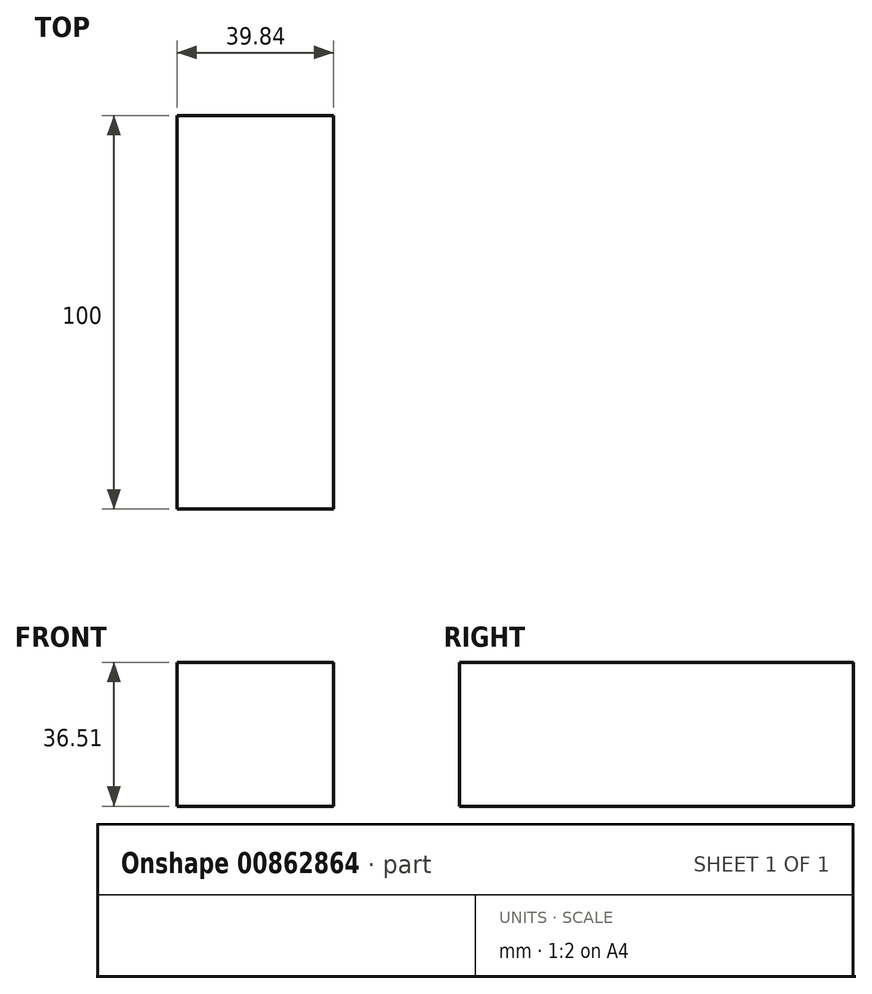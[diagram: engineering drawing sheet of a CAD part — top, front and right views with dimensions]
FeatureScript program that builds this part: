
annotation { "Feature Type Name" : "Feature", "Feature Type Description" : "" }
export const myFeature = defineFeature(function(context is Context, id is Id, definition is map)
    precondition{}
    {
        {
            var Q0;
            Q0=qCreatedBy(makeId("Front.planeOp"),FACE);
            var sketch = newSketch(context, id + "F0", { "sketchPlane" : qUnion([Q0])});
            skLineSegment(sketch, "E0.bottom", {"start": v(-7.34, -18.06) * mm, "end": v(32.5, -18.06) * mm});
            skLineSegment(sketch, "E0.top", {"start": v(-7.34, 18.45) * mm, "end": v(32.5, 18.45) * mm});
            skLineSegment(sketch, "E0.left", {"start": v(-7.34, -18.06) * mm, "end": v(-7.34, 18.45) * mm});
            skLineSegment(sketch, "E0.right", {"start": v(32.5, -18.06) * mm, "end": v(32.5, 18.45) * mm});
            skSolve(sketch);
        }
        {
            var Q0;
            Q0 = qSketchRegion(id + "F0", true);
            extrude(context, id + "F1", {"entities" : qUnion([Q0]), "depth" : 100 * mm, "offsetDistance" : 25.4 * mm});
        }
    });
